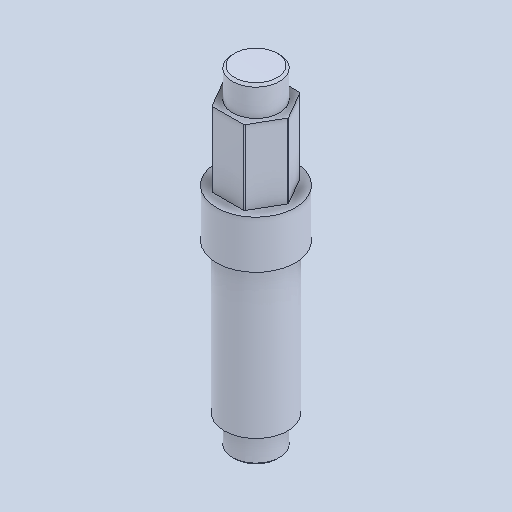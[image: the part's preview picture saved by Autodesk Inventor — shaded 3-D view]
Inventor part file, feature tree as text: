
AUTODESK INVENTOR PART (.ipt)
format: ipt  version: 2024.2 (Build 282272000, 272)  size: 115,712 bytes
history: native  units: in
note: dims shown in document units (in); Inventor stores cm internally (conversion verified against a paired STEP export)
features: chamfer x1
ambient origin geometry x8: Origin, YZ Plane, XZ Plane, XY Plane, X Axis, Y Axis, Z Axis, Center Point
bodies: Solid1 (feature_tree)
feature tree (1):
  chamfer  "Chamfer1"  [1 undecoded]
note: 1 required parameter value undecoded (feature->parameter linkage not recoverable at this tier; creation-order binding heuristic only, values carry confidence <= 0.55)
